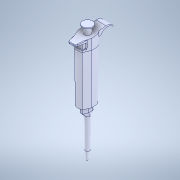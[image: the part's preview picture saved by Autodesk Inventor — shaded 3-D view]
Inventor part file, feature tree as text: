
AUTODESK INVENTOR PART (.ipt)
format: ipt  version: 2022 (Build 260153000, 153)  size: 239,616 bytes
history: mixed  units: in
note: dims shown in document units (in); Inventor stores cm internally (conversion verified against a paired STEP export)
features: revolve x1, imported_body x1
ambient origin geometry x8: Origin, YZ Plane, XZ Plane, XY Plane, X Axis, Y Axis, Z Axis, Center Point
bodies: Solid1 (imported_parasolid)
feature tree (2):
  revolve  "Revolve1"  [1 undecoded]
  imported_body  NMx_Import_Brep_tag  [imported B-rep: ~2 faces, bbox_mm=None]
note: 1 required parameter value undecoded (feature->parameter linkage not recoverable at this tier; creation-order binding heuristic only, values carry confidence <= 0.55)
